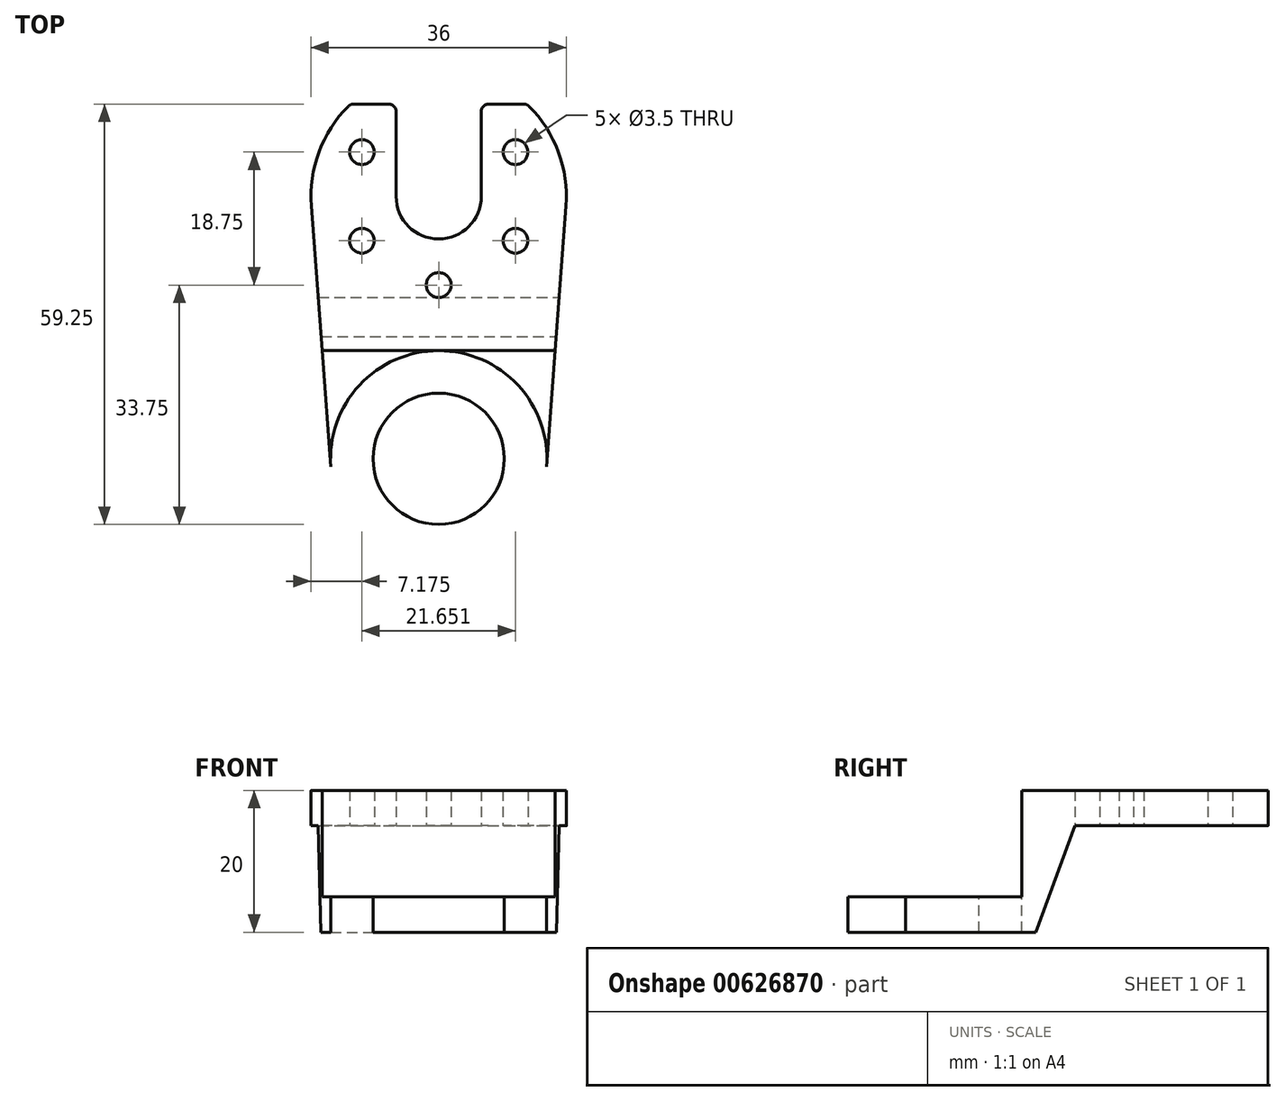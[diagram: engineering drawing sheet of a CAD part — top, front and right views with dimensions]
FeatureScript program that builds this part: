
annotation { "Feature Type Name" : "Feature", "Feature Type Description" : "" }
export const myFeature = defineFeature(function(context is Context, id is Id, definition is map)
    precondition{}
    {
        {
            var Q0;
            Q0=qCreatedBy(makeId("Top.planeOp"),FACE);
            var sketch = newSketch(context, id + "F0", { "sketchPlane" : qUnion([Q0])});
            skArc(sketch, "E0", {"start": v(-12.75, 12.7) * mm, "mid": v(0, -18) * mm, "end": v(12.75, 12.7) * mm});
            skArc(sketch, "E1", {"start": v(-6, 0) * mm, "mid": v(0, -6) * mm, "end": v(6, 0) * mm});
            skCircle(sketch, "E2", {"center": v(0, -12.5) * mm, "radius": 1.75 * mm});
            skCircle(sketch, "E3", {"center": v(10.83, 6.25) * mm, "radius": 1.75 * mm});
            skCircle(sketch, "E4", {"center": v(10.83, -6.25) * mm, "radius": 1.75 * mm});
            skCircle(sketch, "E5", {"center": v(-10.83, 6.25) * mm, "radius": 1.75 * mm});
            skCircle(sketch, "E6", {"center": v(-10.83, -6.25) * mm, "radius": 1.75 * mm});
            skLineSegment(sketch, "E7", {"start": v(-12.04, 13) * mm, "end": v(-7, 13) * mm});
            skLineSegment(sketch, "E8", {"start": v(6, 0) * mm, "end": v(6, 12) * mm});
            skLineSegment(sketch, "E9", {"start": v(-6, 0) * mm, "end": v(-6, 12) * mm});
            skLineSegment(sketch, "E10.trimOffspring", {"start": v(7, 13) * mm, "end": v(12.04, 13) * mm});
            skPoint(sketch, "E11.visualSharp", {"position": v(-6, 13) * mm});
            skArc(sketch, "E11.filletArc", {"start": v(-6, 12) * mm, "mid": v(-6.3, 12.7) * mm, "end": v(-7, 13) * mm});
            skPoint(sketch, "E12.visualSharp", {"position": v(6, 13) * mm});
            skArc(sketch, "E12.filletArc", {"start": v(7, 13) * mm, "mid": v(6.3, 12.7) * mm, "end": v(6, 12) * mm});
            skPoint(sketch, "E13.visualSharp", {"position": v(12.45, 13) * mm});
            skArc(sketch, "E13.filletArc", {"start": v(12.75, 12.7) * mm, "mid": v(12.43, 12.92) * mm, "end": v(12.04, 13) * mm});
            skPoint(sketch, "E14.visualSharp", {"position": v(-12.45, 13) * mm});
            skArc(sketch, "E14.filletArc", {"start": v(-12.04, 13) * mm, "mid": v(-12.43, 12.92) * mm, "end": v(-12.75, 12.7) * mm});
            skPoint(sketch, "E15.end.orphan", {"position": v(-8, 13) * mm});
            skPoint(sketch, "E16.start.orphan", {"position": v(-8, 0) * mm});
            skPoint(sketch, "E17.end.orphan", {"position": v(8, 13) * mm});
            skPoint(sketch, "E17.start.orphan", {"position": v(8, 0) * mm});
            skSolve(sketch);
        }
        {
            var Q0;
            Q0=makeQuery(id+"F0.imprint","IMPRINT",FACE,{"disambiguationData":[TD([[makeQuery(id+"F0.imprint","IMPRINT",EDGE,{"derivedFrom":sQuery(id+"F0.wireOp",EDGE,"E0")}),1.0]])]});
            var Q1;
            Q1=makeQuery(id+"F0.imprint","IMPRINT",FACE,{"disambiguationData":[TD([[makeQuery(id+"F0.imprint","IMPRINT",EDGE,{"derivedFrom":sQuery(id+"F0.wireOp",EDGE,"E1")}),-1.0]])]});
            extrude(context, id + "F1", {"entities" : qUnion([Q0, Q1]), "depth" : 5 * mm, "offsetDistance" : 25 * mm});
        }
        {
            var Q0;
            Q0=qCreatedBy(makeId("Top.planeOp"),FACE);
            var sketch = newSketch(context, id + "F2", { "sketchPlane" : qUnion([Q0])});
            skCircle(sketch, "E18", {"center": v(0, -37) * mm, "radius": 9.25 * mm});
            skCircle(sketch, "E19", {"center": v(0, -37) * mm, "radius": 15.25 * mm});
            skArc(sketch, "E20.0", {"start": v(-12.75, 12.7) * mm, "mid": v(0, -18) * mm, "end": v(12.75, 12.7) * mm});
            skLineSegment(sketch, "E21", {"start": v(-17.95, -1.34) * mm, "end": v(-15.2, -38.13) * mm});
            skLineSegment(sketch, "E22", {"start": v(17.95, -1.34) * mm, "end": v(15.2, -38.13) * mm});
            skLineSegment(sketch, "E23", {"start": v(0, -18) * mm, "end": v(0, -21.75) * mm});
            skLineSegment(sketch, "E24", {"start": v(-16.58, -19.74) * mm, "end": v(16.58, -19.74) * mm});
            skLineSegment(sketch, "E25", {"start": v(0, -21.75) * mm, "end": v(16.43, -21.75) * mm});
            skLineSegment(sketch, "E26", {"start": v(0, -21.75) * mm, "end": v(-16.43, -21.75) * mm});
            skSolve(sketch);
        }
        {
            var Q0;
            {var subQ0=sQuery(id+"F2.wireOp",EDGE,"E21");var subQ1=sQuery(id+"F2.wireOp",EDGE,"E20.0");var subQ2=makeQuery(id+"F2.imprint","INTERSECT",VERTEX,{"derivedFrom":[subQ1,subQ0]});Q0=makeQuery(id+"F2.imprint","IMPRINT",FACE,{"disambiguationData":[TD([[makeQuery(id+"F2.imprint","IMPRINT",EDGE,{"disambiguationData":[TD([[subQ2,-1.0]])],"derivedFrom":subQ1}),-1.0]])]});}
            var Q1;
            {var subQ0=sQuery(id+"F2.wireOp",EDGE,"E22");var subQ1=sQuery(id+"F2.wireOp",EDGE,"E20.0");var subQ2=makeQuery(id+"F2.imprint","INTERSECT",VERTEX,{"derivedFrom":[subQ1,subQ0]});Q1=makeQuery(id+"F2.imprint","IMPRINT",FACE,{"disambiguationData":[TD([[makeQuery(id+"F2.imprint","IMPRINT",EDGE,{"disambiguationData":[TD([[subQ2,1.0]])],"derivedFrom":subQ1}),-1.0]])]});}
            extrude(context, id + "F3", {"entities" : qUnion([Q0, Q1]), "operationType" : NewBodyOperationType.ADD, "depth" : 5 * mm, "offsetDistance" : 25 * mm});
        }
        {
            var Q0;
            {var subQ3=sQuery(id+"F2.wireOp",EDGE,"E26");Q0=makeQuery(id+"F2.imprint","IMPRINT",FACE,{"disambiguationData":[TD([[makeQuery(id+"F2.imprint","IMPRINT",EDGE,{"derivedFrom":subQ3}),-1.0]])]});}
            var Q1;
            {var subQ3=sQuery(id+"F2.wireOp",EDGE,"E25");Q1=makeQuery(id+"F2.imprint","IMPRINT",FACE,{"disambiguationData":[TD([[makeQuery(id+"F2.imprint","IMPRINT",EDGE,{"derivedFrom":subQ3}),1.0]])]});}
            extrude(context, id + "F4", {"entities" : qUnion([Q0, Q1]), "operationType" : NewBodyOperationType.ADD, "oppositeDirection" : true, "depth" : 10 * mm, "offsetDistance" : 25 * mm, "hasSecondDirection" : true, "secondDirectionOppositeDirection" : false, "secondDirectionDepth" : 5 * mm});
        }
        {
            var Q0;
            Q0=makeQuery(id+"F4.opExtrude","CAP_FACE",FACE,{"disambiguationData":[OSD([sQuery(id+"F2.wireOp",EDGE,"E21"),sQuery(id+"F2.wireOp",EDGE,"E22"),sQuery(id+"F2.wireOp",EDGE,"E24"),sQuery(id+"F2.wireOp",EDGE,"E25"),sQuery(id+"F2.wireOp",EDGE,"E26")])],"isStart":false});
            var sketch = newSketch(context, id + "F5", { "sketchPlane" : qUnion([Q0])});
            skLineSegment(sketch, "E27.0", {"start": v(-16.58, 19.74) * mm, "end": v(16.58, 19.74) * mm});
            skLineSegment(sketch, "E27.1", {"start": v(17.95, 1.34) * mm, "end": v(15.2, 38.13) * mm});
            skLineSegment(sketch, "E27.2", {"start": v(0, 21.75) * mm, "end": v(16.43, 21.75) * mm});
            skLineSegment(sketch, "E27.3", {"start": v(0, 21.75) * mm, "end": v(-16.43, 21.75) * mm});
            skLineSegment(sketch, "E27.4", {"start": v(-17.95, 1.34) * mm, "end": v(-15.2, 38.13) * mm});
            skCircle(sketch, "E27.5", {"center": v(0, 37) * mm, "radius": 15.25 * mm});
            skCircle(sketch, "E27.6", {"center": v(0, 37) * mm, "radius": 9.25 * mm});
            skSolve(sketch);
        }
        {
            var Q0;
            {var subQ3=sQuery(id+"F5.wireOp",EDGE,"E27.0");Q0=makeQuery(id+"F5.imprint","IMPRINT",FACE,{"disambiguationData":[TD([[makeQuery(id+"F5.imprint","IMPRINT",EDGE,{"derivedFrom":subQ3}),1.0]])]});}
            var Q1;
            {var subQ0=sQuery(id+"F5.wireOp",EDGE,"E27.2");Q1=makeQuery(id+"F5.imprint","IMPRINT",FACE,{"disambiguationData":[TD([[makeQuery(id+"F5.imprint","IMPRINT",EDGE,{"derivedFrom":subQ0}),-1.0]])]});}
            var Q2;
            {var subQ0=sQuery(id+"F5.wireOp",EDGE,"E27.3");Q2=makeQuery(id+"F5.imprint","IMPRINT",FACE,{"disambiguationData":[TD([[makeQuery(id+"F5.imprint","IMPRINT",EDGE,{"derivedFrom":subQ0}),-1.0]])]});}
            var Q3;
            Q3=makeQuery(id+"F5.imprint","IMPRINT",FACE,{"disambiguationData":[TD([[makeQuery(id+"F5.imprint","IMPRINT",EDGE,{"derivedFrom":sQuery(id+"F5.wireOp",EDGE,"E27.6")}),1.0]])]});
            extrude(context, id + "F6", {"entities" : qUnion([Q0, Q1, Q2, Q3]), "operationType" : NewBodyOperationType.ADD, "depth" : 5 * mm, "offsetDistance" : 25 * mm});
        }
        {
            var Q0;
            Q0=sQuery(id+"F2.wireOp",EDGE,"E23");
            cPoint(context, id + "F7", {"entities" : qUnion([Q0]), "parameter" : 0.5});
        }
        {
            var Q0;
            Q0=makeQuery(id+"F6.opExtrude","CAP_EDGE",EDGE,{"disambiguationData":[OSD([sQuery(id+"F5.wireOp",EDGE,"E27.0")])],"isStart":false});
            cPoint(context, id + "F8", {"entities" : qUnion([Q0]), "parameter" : 0.5});
        }
        {
            var Q0;
            Q0=sQuery(id+"F2.wireOp",VERTEX,"E23.start");
            var Q1;
            Q1 = qCreatedBy(id + "F7" ,VERTEX);
            var Q2;
            Q2 = qCreatedBy(id + "F8" ,VERTEX);
            cPlane(context, id + "F9", {"entities" : qUnion([Q0, Q1, Q2]), "cplaneType" : CPlaneType.THREE_POINT, "offset" : 25 * mm, "width" : 150 * mm, "height" : 150 * mm});
        }
        {
            var Q0;
            Q0=qCreatedBy(makeId("Front.planeOp"),FACE);
            var sketch = newSketch(context, id + "F10", { "sketchPlane" : qUnion([Q0])});
            skLineSegment(sketch, "E28", {"start": v(0, -38.86) * mm, "end": v(0, 28.7) * mm});
            skSolve(sketch);
        }
        {
            var Q0;
            Q0=qCreatedBy(id+"F9.planeOp",FACE);
            var sketch = newSketch(context, id + "F11", { "sketchPlane" : qUnion([Q0])});
            skLineSegment(sketch, "E29.0", {"start": v(1.34, 0) * mm, "end": v(38.13, 0) * mm});
            skLineSegment(sketch, "E30.0", {"start": v(19.74, -15) * mm, "end": v(38.13, -15) * mm});
            skLineSegment(sketch, "E31.0", {"start": v(10.75, 0) * mm, "end": v(14.25, 0) * mm});
            skLineSegment(sketch, "E32", {"start": v(19.74, 0) * mm, "end": v(19.74, -15) * mm});
            skLineSegment(sketch, "E33", {"start": v(14.25, 0) * mm, "end": v(19.74, -15) * mm});
            skSolve(sketch);
        }
        {
            var Q0;
            {var subQ2=sQuery(id+"F11.wireOp",EDGE,"E32");Q0=makeQuery(id+"F11.imprint","IMPRINT",FACE,{"disambiguationData":[TD([[makeQuery(id+"F11.imprint","IMPRINT",EDGE,{"derivedFrom":subQ2}),-1.0]])]});}
            var Q1;
            {var subQ0=sQuery(id+"F2.wireOp",EDGE,"E21");Q1=makeQuery(id+"F6.boolean.opBoolean","MERGE",FACE,{"derivedFrom":[makeQuery(id+"F4.boolean.opBoolean","MERGE",FACE,{"derivedFrom":[makeQuery(id+"F3.opExtrude","SWEPT_FACE",FACE,{"disambiguationData":[OSD([subQ0])]}),makeQuery(id+"F4.opExtrude","SWEPT_FACE",FACE,{"disambiguationData":[OSD([subQ0])]})]}),makeQuery(id+"F6.opExtrude","SWEPT_FACE",FACE,{"disambiguationData":[OSD([sQuery(id+"F5.wireOp",EDGE,"E27.4")])]})]});}
            var Q2;
            {var subQ0=sQuery(id+"F2.wireOp",EDGE,"E22");Q2=makeQuery(id+"F6.boolean.opBoolean","MERGE",FACE,{"derivedFrom":[makeQuery(id+"F4.boolean.opBoolean","MERGE",FACE,{"derivedFrom":[makeQuery(id+"F3.opExtrude","SWEPT_FACE",FACE,{"disambiguationData":[OSD([subQ0])]}),makeQuery(id+"F4.opExtrude","SWEPT_FACE",FACE,{"disambiguationData":[OSD([subQ0])]})]}),makeQuery(id+"F6.opExtrude","SWEPT_FACE",FACE,{"disambiguationData":[OSD([sQuery(id+"F5.wireOp",EDGE,"E27.1")])]})]});}
            extrude(context, id + "F12", {"entities" : qUnion([Q0]), "operationType" : NewBodyOperationType.ADD, "endBound" : BoundingType.UP_TO_SURFACE, "depth" : 25 * mm, "endBoundEntityFace" : qUnion([Q1]), "offsetDistance" : 25 * mm, "hasSecondDirection" : true, "secondDirectionBound" : SecondDirectionBoundingType.UP_TO_SURFACE, "secondDirectionOppositeDirection" : true, "secondDirectionDepth" : 25 * mm, "secondDirectionBoundEntityFace" : qUnion([Q2])});
        }
    });
